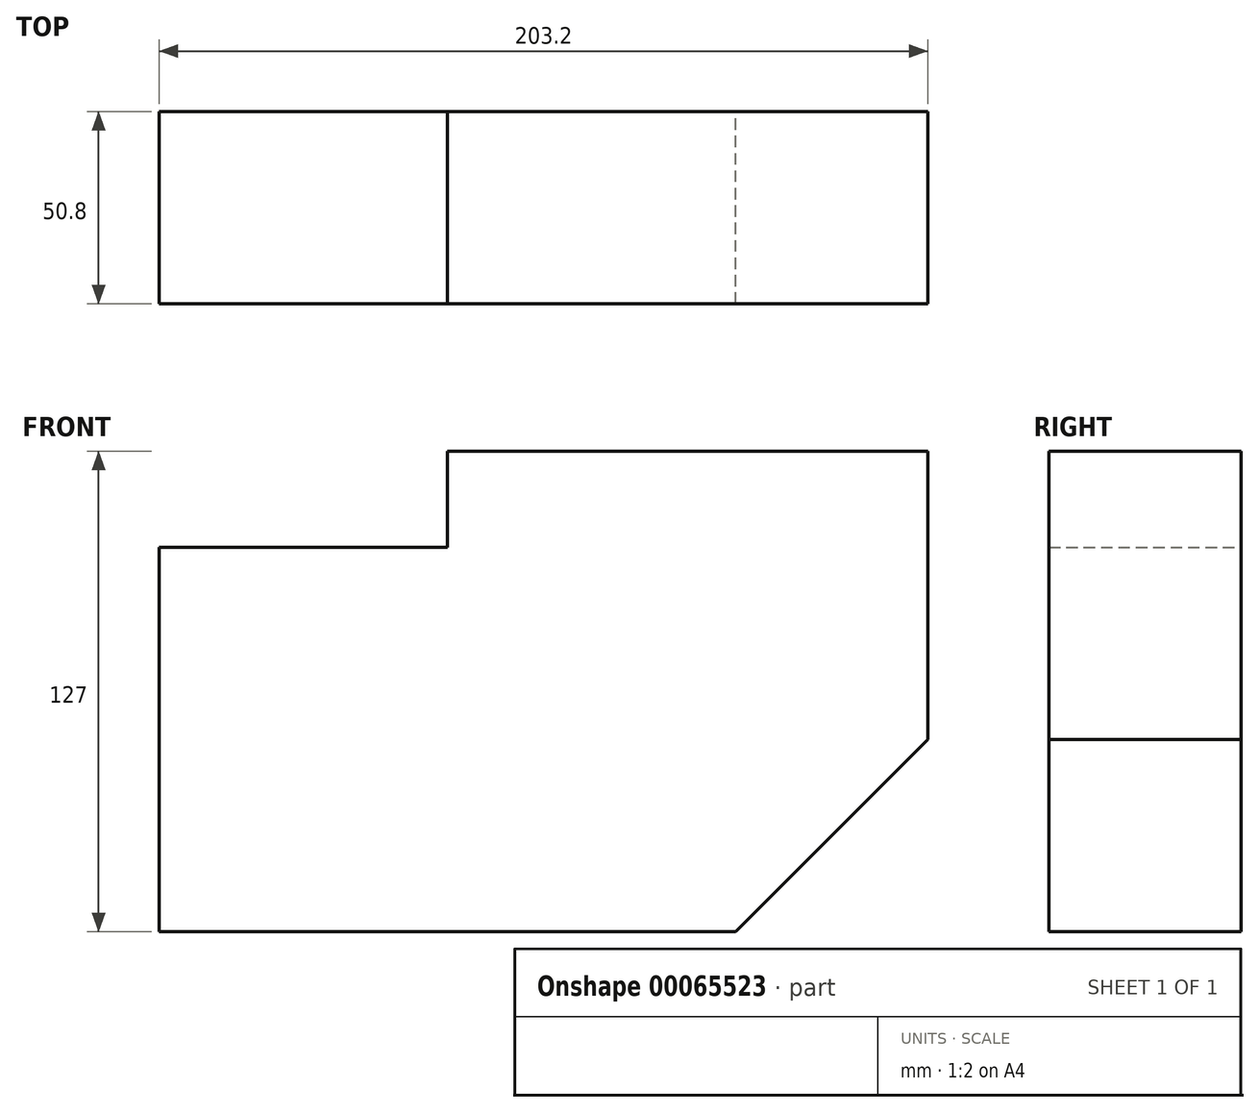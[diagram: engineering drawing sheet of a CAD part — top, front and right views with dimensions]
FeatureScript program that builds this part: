
annotation { "Feature Type Name" : "Feature", "Feature Type Description" : "" }
export const myFeature = defineFeature(function(context is Context, id is Id, definition is map)
    precondition{}
    {
        {
            var Q0;
            Q0=qCreatedBy(makeId("Front.planeOp"),FACE);
            var sketch = newSketch(context, id + "F0", { "sketchPlane" : qUnion([Q0])});
            skLineSegment(sketch, "E0", {"start": v(0, 0) * mm, "end": v(0, 101.6) * mm});
            skLineSegment(sketch, "E1", {"start": v(0, 101.6) * mm, "end": v(76.2, 101.6) * mm});
            skLineSegment(sketch, "E2", {"start": v(76.2, 101.6) * mm, "end": v(76.2, 127) * mm});
            skLineSegment(sketch, "E3", {"start": v(76.2, 127) * mm, "end": v(203.2, 127) * mm});
            skLineSegment(sketch, "E4", {"start": v(203.2, 127) * mm, "end": v(203.2, 50.8) * mm});
            skLineSegment(sketch, "E5", {"start": v(203.2, 50.8) * mm, "end": v(152.4, 0) * mm});
            skLineSegment(sketch, "E6", {"start": v(152.4, 0) * mm, "end": v(0, 0) * mm});
            skSolve(sketch);
        }
        {
            var Q0;
            Q0=makeQuery(id+"F0.imprint","IMPRINT",FACE,{"disambiguationData":[TD([[makeQuery(id+"F0.imprint","IMPRINT",EDGE,{"derivedFrom":sQuery(id+"F0.wireOp",EDGE,"E0")}),-1.0]])]});
            extrude(context, id + "F1", {"entities" : qUnion([Q0]), "depth" : 50.8 * mm});
        }
    });
